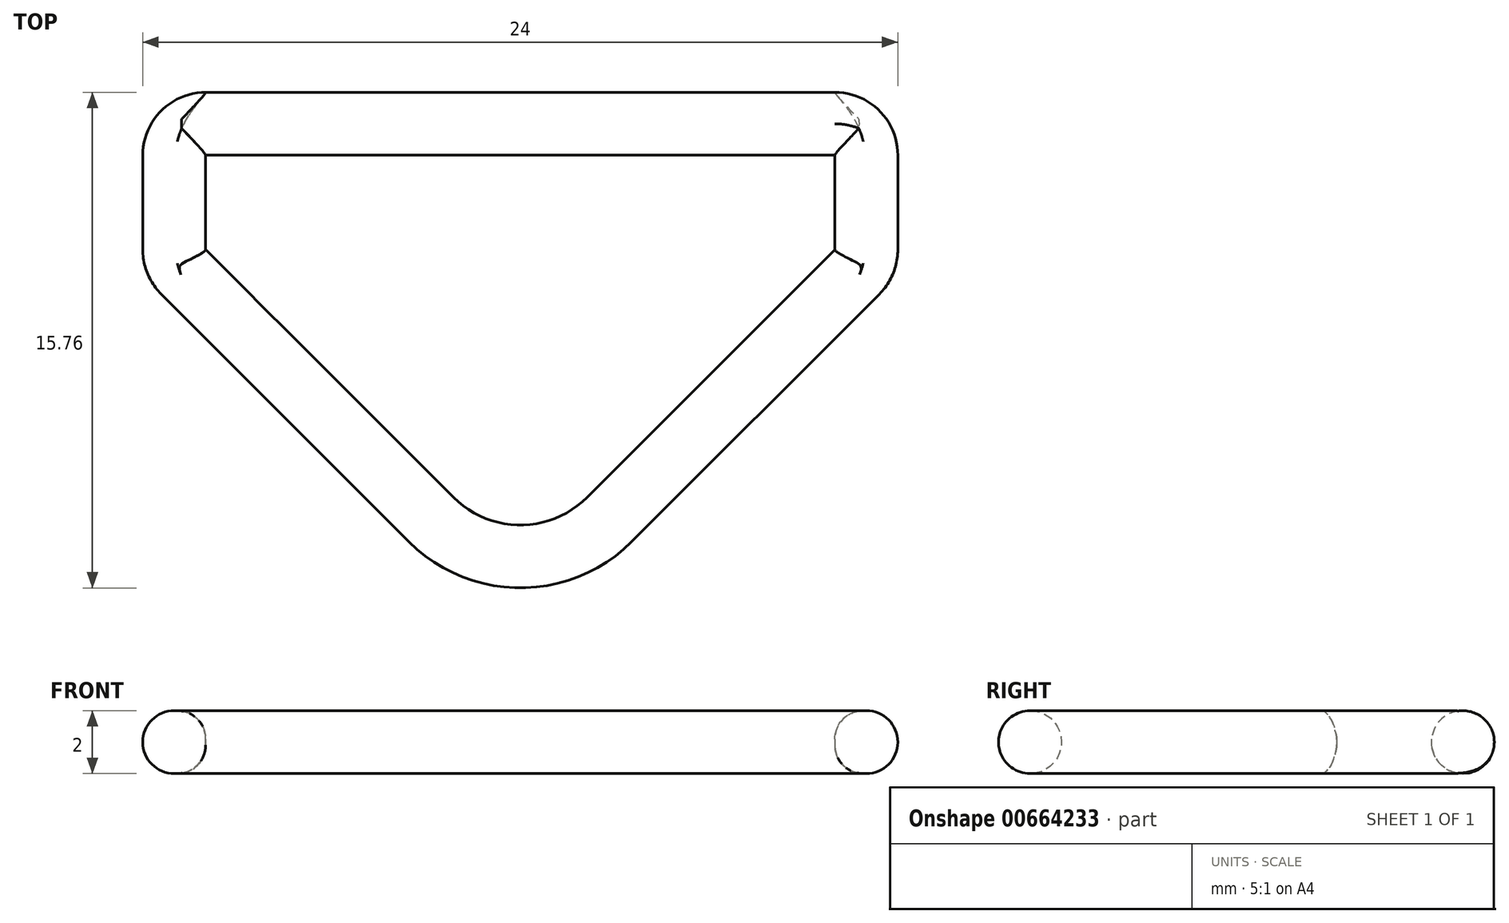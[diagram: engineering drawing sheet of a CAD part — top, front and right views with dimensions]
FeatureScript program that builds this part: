
annotation { "Feature Type Name" : "Feature", "Feature Type Description" : "" }
export const myFeature = defineFeature(function(context is Context, id is Id, definition is map)
    precondition{}
    {
        {
            var Q0;
            Q0=qCreatedBy(makeId("Top.planeOp"),FACE);
            var sketch = newSketch(context, id + "F0", { "sketchPlane" : qUnion([Q0])});
            skLineSegment(sketch, "E0.bottom", {"start": v(-10, 1.5) * mm, "end": v(10, 1.5) * mm});
            skLineSegment(sketch, "E0.top", {"start": v(-10, -1.5) * mm, "end": v(10, -1.5) * mm});
            skLineSegment(sketch, "E0.left", {"start": v(-10, 1.5) * mm, "end": v(-10, -1.5) * mm});
            skLineSegment(sketch, "E0.right", {"start": v(10, 1.5) * mm, "end": v(10, -1.5) * mm});
            skPoint(sketch, "E0.middle", {"position": v(0, 0) * mm});
            skLineSegment(sketch, "E1.bottom", {"start": v(-10, 3.5) * mm, "end": v(10, 3.5) * mm});
            skLineSegment(sketch, "E1.left", {"start": v(-10, 3.5) * mm, "end": v(-10, 1.5) * mm});
            skLineSegment(sketch, "E1.right", {"start": v(10, 3.5) * mm, "end": v(10, 1.5) * mm});
            skLineSegment(sketch, "E2.bottom", {"start": v(-12, 1.5) * mm, "end": v(-10, 1.5) * mm});
            skLineSegment(sketch, "E2.top", {"start": v(-12, -1.5) * mm, "end": v(-10, -1.5) * mm});
            skLineSegment(sketch, "E2.left", {"start": v(-12, 1.5) * mm, "end": v(-12, -1.5) * mm});
            skLineSegment(sketch, "E3.bottom", {"start": v(10, 1.5) * mm, "end": v(12, 1.5) * mm});
            skLineSegment(sketch, "E3.top", {"start": v(10, -1.5) * mm, "end": v(12, -1.5) * mm});
            skLineSegment(sketch, "E3.right", {"start": v(12, 1.5) * mm, "end": v(12, -1.5) * mm});
            skLineSegment(sketch, "E4.bottom", {"start": v(0, -1.5) * mm, "end": v(10, -1.5) * mm});
            skLineSegment(sketch, "E5.bottom", {"start": v(-10, -1.5) * mm, "end": v(0, -1.5) * mm});
            skLineSegment(sketch, "E6", {"start": v(-10, -1.5) * mm, "end": v(-2.12, -9.38) * mm});
            skLineSegment(sketch, "E7", {"start": v(2.12, -9.38) * mm, "end": v(10, -1.5) * mm});
            skLineSegment(sketch, "E8", {"start": v(-10, -1.5) * mm, "end": v(-11.41, -2.91) * mm});
            skLineSegment(sketch, "E9", {"start": v(-11.41, -2.91) * mm, "end": v(-3.54, -10.8) * mm});
            skLineSegment(sketch, "E10", {"start": v(10, -1.5) * mm, "end": v(11.41, -2.91) * mm});
            skLineSegment(sketch, "E11", {"start": v(11.41, -2.91) * mm, "end": v(3.54, -10.8) * mm});
            skLineSegment(sketch, "E12.bottom", {"start": v(-12, 3.5) * mm, "end": v(-10, 3.5) * mm});
            skLineSegment(sketch, "E12.left", {"start": v(-12, 3.5) * mm, "end": v(-12, 1.5) * mm});
            skLineSegment(sketch, "E13.bottom", {"start": v(10, 3.5) * mm, "end": v(12, 3.5) * mm});
            skLineSegment(sketch, "E13.right", {"start": v(12, 3.5) * mm, "end": v(12, 1.5) * mm});
            skLineSegment(sketch, "E14", {"start": v(12, -1.5) * mm, "end": v(12, -2.33) * mm});
            skLineSegment(sketch, "E15", {"start": v(11.41, -2.91) * mm, "end": v(12, -2.33) * mm});
            skPoint(sketch, "E16", {"position": v(12, -2.33) * mm});
            skLineSegment(sketch, "E17", {"start": v(-12, -1.5) * mm, "end": v(-12, -2.33) * mm});
            skLineSegment(sketch, "E18", {"start": v(-11.41, -2.91) * mm, "end": v(-12, -2.33) * mm});
            skPoint(sketch, "E19", {"position": v(-12, -2.33) * mm});
            skLineSegment(sketch, "E20", {"start": v(-3.54, -10.8) * mm, "end": v(-2.12, -9.38) * mm});
            skLineSegment(sketch, "E21", {"start": v(2.12, -9.38) * mm, "end": v(3.54, -10.8) * mm});
            skCircle(sketch, "E22", {"center": v(0, -7.26) * mm, "radius": 3 * mm});
            skArc(sketch, "E23", {"start": v(-3.54, -10.8) * mm, "mid": v(0, -12.26) * mm, "end": v(3.54, -10.8) * mm});
            skSolve(sketch);
        }
        {
            var Q0;
            Q0=makeQuery(id+"F0.imprint","IMPRINT",FACE,{"disambiguationData":[TD([[makeQuery(id+"F0.imprint","IMPRINT",EDGE,{"derivedFrom":sQuery(id+"F0.wireOp",EDGE,"E12.bottom")}),-1.0]])]});
            var Q1;
            Q1=makeQuery(id+"F0.imprint","IMPRINT",FACE,{"disambiguationData":[TD([[makeQuery(id+"F0.imprint","IMPRINT",EDGE,{"derivedFrom":sQuery(id+"F0.wireOp",EDGE,"E1.bottom")}),-1.0]])]});
            var Q2;
            Q2=makeQuery(id+"F0.imprint","IMPRINT",FACE,{"disambiguationData":[TD([[makeQuery(id+"F0.imprint","IMPRINT",EDGE,{"derivedFrom":sQuery(id+"F0.wireOp",EDGE,"E13.bottom")}),-1.0]])]});
            var Q3;
            Q3=makeQuery(id+"F0.imprint","IMPRINT",FACE,{"disambiguationData":[TD([[makeQuery(id+"F0.imprint","IMPRINT",EDGE,{"derivedFrom":sQuery(id+"F0.wireOp",EDGE,"E3.top")}),1.0]])]});
            var Q4;
            Q4=makeQuery(id+"F0.imprint","IMPRINT",FACE,{"disambiguationData":[TD([[makeQuery(id+"F0.imprint","IMPRINT",EDGE,{"derivedFrom":sQuery(id+"F0.wireOp",EDGE,"E3.top")}),-1.0]])]});
            var Q5;
            Q5=makeQuery(id+"F0.imprint","IMPRINT",FACE,{"disambiguationData":[TD([[makeQuery(id+"F0.imprint","IMPRINT",EDGE,{"derivedFrom":sQuery(id+"F0.wireOp",EDGE,"E7")}),-1.0]])]});
            var Q6;
            {var subQ0=sQuery(id+"F0.wireOp",EDGE,"E20");Q6=makeQuery(id+"F0.imprint","IMPRINT",FACE,{"disambiguationData":[TD([[makeQuery(id+"F0.imprint","IMPRINT",EDGE,{"derivedFrom":subQ0}),-1.0]])]});}
            var Q7;
            Q7=makeQuery(id+"F0.imprint","IMPRINT",FACE,{"disambiguationData":[TD([[makeQuery(id+"F0.imprint","IMPRINT",EDGE,{"derivedFrom":sQuery(id+"F0.wireOp",EDGE,"E6")}),-1.0]])]});
            var Q8;
            Q8=makeQuery(id+"F0.imprint","IMPRINT",FACE,{"disambiguationData":[TD([[makeQuery(id+"F0.imprint","IMPRINT",EDGE,{"derivedFrom":sQuery(id+"F0.wireOp",EDGE,"E2.top")}),-1.0]])]});
            var Q9;
            Q9=makeQuery(id+"F0.imprint","IMPRINT",FACE,{"disambiguationData":[TD([[makeQuery(id+"F0.imprint","IMPRINT",EDGE,{"derivedFrom":sQuery(id+"F0.wireOp",EDGE,"E2.top")}),1.0]])]});
            var Q10;
            Q10=makeQuery(id+"F0.imprint","IMPRINT",FACE,{"disambiguationData":[TD([[makeQuery(id+"F0.imprint","IMPRINT",EDGE,{"derivedFrom":sQuery(id+"F0.wireOp",EDGE,"E4.bottom")}),-1.0]])]});
            extrude(context, id + "F1", {"entities" : qUnion([Q0, Q1, Q2, Q3, Q4, Q5, Q6, Q7, Q8, Q9, Q10]), "depth" : 2 * mm, "offsetDistance" : 25 * mm});
        }
        {
            var Q0;
            Q0=makeQuery(id+"F1.opExtrude","SWEPT_EDGE",EDGE,{"disambiguationData":[OSD([sQuery(id+"F0.wireOp",EDGE,"E12.bottom"),sQuery(id+"F0.wireOp",EDGE,"E12.left")])]});
            var Q1;
            Q1=makeQuery(id+"F1.opExtrude","SWEPT_EDGE",EDGE,{"disambiguationData":[OSD([sQuery(id+"F0.wireOp",EDGE,"E17"),sQuery(id+"F0.wireOp",EDGE,"E18")])]});
            var Q2;
            Q2=makeQuery(id+"F1.opExtrude","SWEPT_EDGE",EDGE,{"disambiguationData":[OSD([sQuery(id+"F0.wireOp",EDGE,"E14"),sQuery(id+"F0.wireOp",EDGE,"E15")])]});
            var Q3;
            Q3=makeQuery(id+"F1.opExtrude","SWEPT_EDGE",EDGE,{"disambiguationData":[OSD([sQuery(id+"F0.wireOp",EDGE,"E13.bottom"),sQuery(id+"F0.wireOp",EDGE,"E13.right")])]});
            fillet(context, id + "F2", {"entities" : qUnion([Q0, Q1, Q2, Q3]), "radius" : 2 * mm, "tangentPropagation" : true, "allowEdgeOverflow" : false});
        }
        {
            var Q0;
            Q0=makeQuery(id+"F1.opExtrude","CAP_EDGE",EDGE,{"disambiguationData":[OSD([sQuery(id+"F0.wireOp",EDGE,"E4.bottom"),sQuery(id+"F0.wireOp",EDGE,"E5.bottom")])],"isStart":false});
            var Q1;
            Q1=makeQuery(id+"F1.opExtrude","CAP_EDGE",EDGE,{"disambiguationData":[OSD([sQuery(id+"F0.wireOp",EDGE,"E0.bottom")])],"isStart":false});
            var Q2;
            Q2=makeQuery(id+"F1.opExtrude","CAP_EDGE",EDGE,{"disambiguationData":[OSD([sQuery(id+"F0.wireOp",EDGE,"E4.bottom"),sQuery(id+"F0.wireOp",EDGE,"E5.bottom")])],"isStart":true});
            var Q3;
            Q3=makeQuery(id+"F1.opExtrude","CAP_EDGE",EDGE,{"disambiguationData":[OSD([sQuery(id+"F0.wireOp",EDGE,"E0.bottom")])],"isStart":true});
            var Q4;
            Q4=makeQuery(id+"F1.opExtrude","CAP_EDGE",EDGE,{"disambiguationData":[OSD([sQuery(id+"F0.wireOp",EDGE,"E22")])],"isStart":true});
            var Q5;
            Q5=makeQuery(id+"F1.opExtrude","CAP_EDGE",EDGE,{"disambiguationData":[OSD([sQuery(id+"F0.wireOp",EDGE,"E22")])],"isStart":false});
            var Q6;
            Q6=makeQuery(id+"F1.opExtrude","CAP_EDGE",EDGE,{"disambiguationData":[OSD([sQuery(id+"F0.wireOp",EDGE,"E11"),sQuery(id+"F0.wireOp",EDGE,"E15")])],"isStart":false});
            var Q7;
            Q7=makeQuery(id+"F1.opExtrude","CAP_EDGE",EDGE,{"disambiguationData":[OSD([sQuery(id+"F0.wireOp",EDGE,"E11"),sQuery(id+"F0.wireOp",EDGE,"E15")])],"isStart":true});
            fillet(context, id + "F3", {"entities" : qUnion([Q0, Q1, Q2, Q3, Q4, Q5, Q6, Q7]), "radius" : 1 * mm, "tangentPropagation" : true, "allowEdgeOverflow" : false});
        }
        {
            var Q0;
            Q0=makeQuery(id+"F1.opExtrude","CAP_EDGE",EDGE,{"disambiguationData":[OSD([sQuery(id+"F0.wireOp",EDGE,"E0.left")])],"isStart":false});
            var Q1;
            Q1=makeQuery(id+"F1.opExtrude","CAP_EDGE",EDGE,{"disambiguationData":[OSD([sQuery(id+"F0.wireOp",EDGE,"E0.left")])],"isStart":true});
            var Q2;
            Q2=makeQuery(id+"F1.opExtrude","CAP_EDGE",EDGE,{"disambiguationData":[OSD([sQuery(id+"F0.wireOp",EDGE,"E0.right")])],"isStart":false});
            var Q3;
            Q3=makeQuery(id+"F1.opExtrude","CAP_EDGE",EDGE,{"disambiguationData":[OSD([sQuery(id+"F0.wireOp",EDGE,"E0.right")])],"isStart":true});
            fillet(context, id + "F4", {"entities" : qUnion([Q0, Q1, Q2, Q3]), "radius" : 0.9 * mm, "tangentPropagation" : true, "allowEdgeOverflow" : false});
        }
    });
